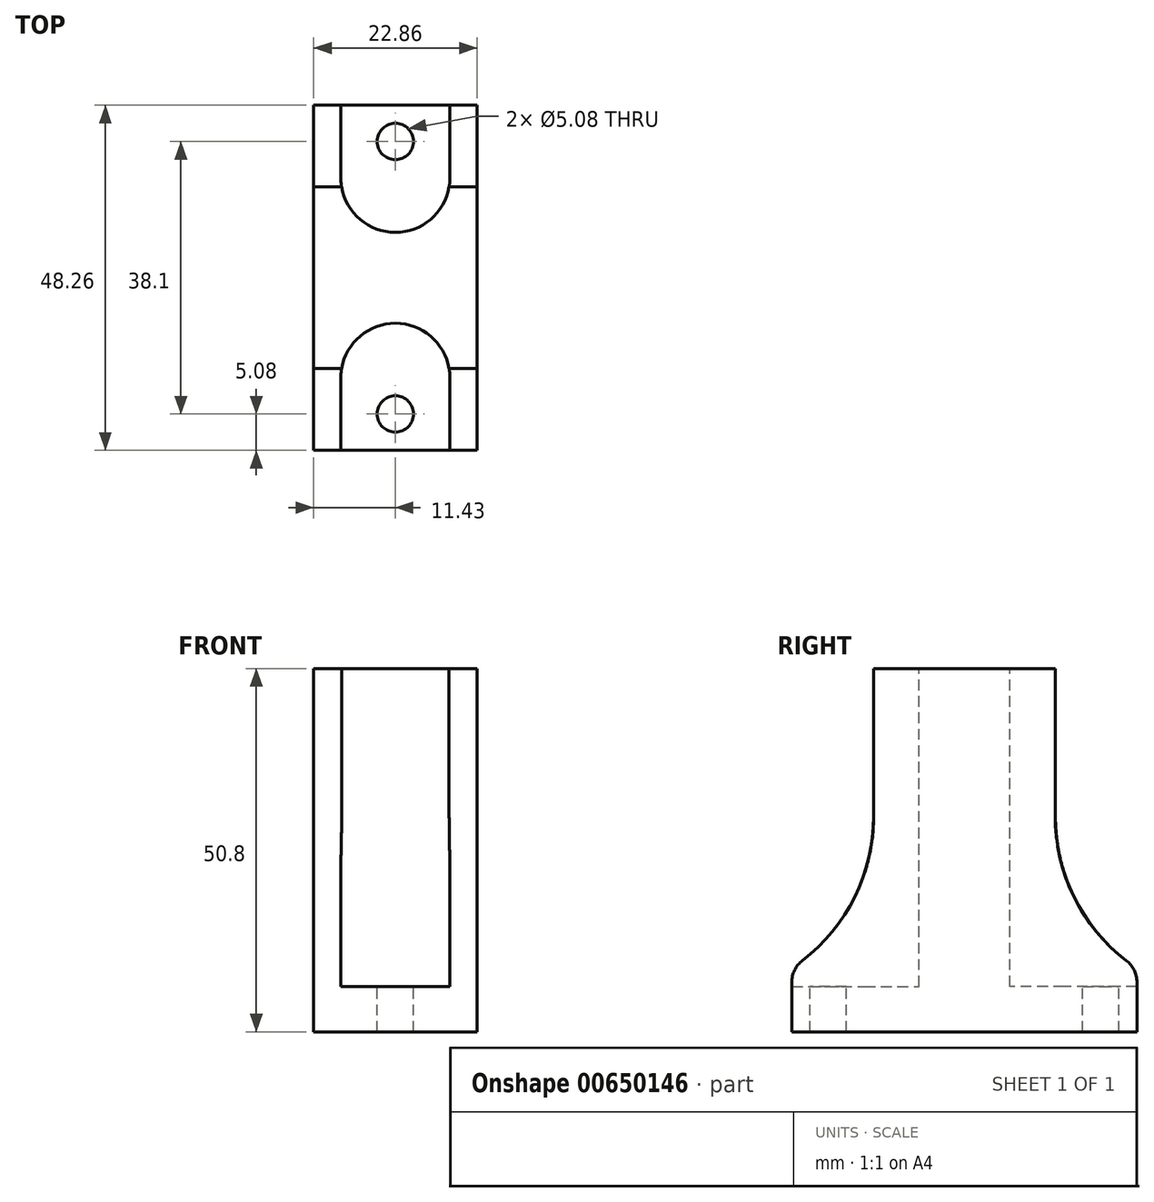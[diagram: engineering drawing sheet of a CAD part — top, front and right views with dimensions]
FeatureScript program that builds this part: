
annotation { "Feature Type Name" : "Feature", "Feature Type Description" : "" }
export const myFeature = defineFeature(function(context is Context, id is Id, definition is map)
    precondition{}
    {
        {
            var Q0;
            Q0=qCreatedBy(makeId("Top.planeOp"),FACE);
            var sketch = newSketch(context, id + "F0", { "sketchPlane" : qUnion([Q0])});
            skLineSegment(sketch, "E0.bottom", {"start": v(-11.43, 24.13) * mm, "end": v(11.43, 24.13) * mm});
            skLineSegment(sketch, "E0.top", {"start": v(-11.43, -24.13) * mm, "end": v(11.43, -24.13) * mm});
            skLineSegment(sketch, "E0.left", {"start": v(-11.43, 24.13) * mm, "end": v(-11.43, -24.13) * mm});
            skLineSegment(sketch, "E0.right", {"start": v(11.43, 24.13) * mm, "end": v(11.43, -24.13) * mm});
            skLineSegment(sketch, "E1", {"start": v(-11.43, -24.13) * mm, "end": v(11.43, 24.13) * mm, "construction": true});
            skSolve(sketch);
        }
        {
            var Q0;
            Q0 = qSketchRegion(id + "F0", true);
            extrude(context, id + "F1", {"entities" : qUnion([Q0]), "depth" : 50.8 * mm, "offsetDistance" : 25.4 * mm});
        }
        {
            var Q0;
            Q0=makeQuery(id+"F1.opExtrude","CAP_FACE",FACE,{"disambiguationData":[OSD([sQuery(id+"F0.wireOp",EDGE,"E0.bottom"),sQuery(id+"F0.wireOp",EDGE,"E0.top"),sQuery(id+"F0.wireOp",EDGE,"E0.left"),sQuery(id+"F0.wireOp",EDGE,"E0.right")])],"isStart":false});
            var sketch = newSketch(context, id + "F2", { "sketchPlane" : qUnion([Q0])});
            skLineSegment(sketch, "E2.bottom", {"start": v(-11.43, 12.7) * mm, "end": v(11.43, 12.7) * mm, "construction": true});
            skLineSegment(sketch, "E2.top", {"start": v(-11.43, -12.7) * mm, "end": v(11.43, -12.7) * mm, "construction": true});
            skLineSegment(sketch, "E2.left", {"start": v(-11.43, 12.7) * mm, "end": v(-11.43, -12.7) * mm, "construction": true});
            skLineSegment(sketch, "E2.right", {"start": v(11.43, 12.7) * mm, "end": v(11.43, -12.7) * mm, "construction": true});
            skLineSegment(sketch, "E3", {"start": v(-11.43, 12.7) * mm, "end": v(11.43, -12.7) * mm, "construction": true});
            skLineSegment(sketch, "E4.bottom", {"start": v(-11.43, 24.13) * mm, "end": v(11.43, 24.13) * mm});
            skLineSegment(sketch, "E4.top", {"start": v(-11.43, 12.7) * mm, "end": v(11.43, 12.7) * mm});
            skLineSegment(sketch, "E4.left", {"start": v(-11.43, 24.13) * mm, "end": v(-11.43, 12.7) * mm});
            skLineSegment(sketch, "E4.right", {"start": v(11.43, 24.13) * mm, "end": v(11.43, 12.7) * mm});
            skLineSegment(sketch, "E5.bottom", {"start": v(-11.43, -24.13) * mm, "end": v(11.43, -24.13) * mm});
            skLineSegment(sketch, "E5.top", {"start": v(-11.43, -12.7) * mm, "end": v(11.43, -12.7) * mm});
            skLineSegment(sketch, "E5.left", {"start": v(-11.43, -24.13) * mm, "end": v(-11.43, -12.7) * mm});
            skLineSegment(sketch, "E5.right", {"start": v(11.43, -24.13) * mm, "end": v(11.43, -12.7) * mm});
            skLineSegment(sketch, "E6.bottom", {"start": v(-7.62, 12.7) * mm, "end": v(7.62, 12.7) * mm});
            skLineSegment(sketch, "E6.top", {"start": v(-7.62, 6.35) * mm, "end": v(7.62, 6.35) * mm});
            skLineSegment(sketch, "E6.left", {"start": v(-7.62, 12.7) * mm, "end": v(-7.62, 6.35) * mm});
            skLineSegment(sketch, "E6.right", {"start": v(7.62, 12.7) * mm, "end": v(7.62, 6.35) * mm});
            skLineSegment(sketch, "E7.bottom", {"start": v(-7.62, -12.7) * mm, "end": v(7.62, -12.7) * mm});
            skLineSegment(sketch, "E7.top", {"start": v(-7.62, -6.35) * mm, "end": v(7.62, -6.35) * mm});
            skLineSegment(sketch, "E7.left", {"start": v(-7.62, -12.7) * mm, "end": v(-7.62, -6.35) * mm});
            skLineSegment(sketch, "E7.right", {"start": v(7.62, -12.7) * mm, "end": v(7.62, -6.35) * mm});
            skSolve(sketch);
        }
        {
            var Q0;
            Q0 = qSketchRegion(id + "F2", true);
            extrude(context, id + "F3", {"entities" : qUnion([Q0]), "operationType" : NewBodyOperationType.REMOVE, "oppositeDirection" : true, "depth" : 41.9 * mm, "offsetDistance" : 25.4 * mm});
        }
        {
            var Q0;
            {var subQ0=sQuery(id+"F2.wireOp",EDGE,"E5.top");Q0=makeQuery(id+"F3.boolean.opBoolean","COPY",EDGE,{"derivedFrom":makeQuery(id+"F3.opExtrude","CAP_EDGE",EDGE,{"disambiguationData":[OSD([subQ0]),TDD([makeQuery(id+"F2.imprint","IMPRINT",EDGE,{"disambiguationData":[TD([[makeQuery(id+"F2.imprint","INTERSECT",VERTEX,{"derivedFrom":[makeQuery(id+"F1.opExtrude","CAP_EDGE",EDGE,{"disambiguationData":[OSD([sQuery(id+"F0.wireOp",EDGE,"E0.left")])],"isStart":false}),subQ0,sQuery(id+"F2.wireOp",EDGE,"E5.left")]}),-1.0]])],"derivedFrom":subQ0})])],"isStart":false})});}
            var Q1;
            {var subQ0=sQuery(id+"F2.wireOp",EDGE,"E5.top");Q1=makeQuery(id+"F3.boolean.opBoolean","COPY",EDGE,{"derivedFrom":makeQuery(id+"F3.opExtrude","CAP_EDGE",EDGE,{"disambiguationData":[OSD([subQ0]),TDD([makeQuery(id+"F2.imprint","IMPRINT",EDGE,{"disambiguationData":[TD([[makeQuery(id+"F2.imprint","INTERSECT",VERTEX,{"derivedFrom":[makeQuery(id+"F1.opExtrude","CAP_EDGE",EDGE,{"disambiguationData":[OSD([sQuery(id+"F0.wireOp",EDGE,"E0.right")])],"isStart":false}),subQ0,sQuery(id+"F2.wireOp",EDGE,"E5.right")]}),1.0]])],"derivedFrom":subQ0})])],"isStart":false})});}
            var Q2;
            {var subQ0=sQuery(id+"F2.wireOp",EDGE,"E4.top");Q2=makeQuery(id+"F3.boolean.opBoolean","COPY",EDGE,{"derivedFrom":makeQuery(id+"F3.opExtrude","CAP_EDGE",EDGE,{"disambiguationData":[OSD([subQ0]),TDD([makeQuery(id+"F2.imprint","IMPRINT",EDGE,{"disambiguationData":[TD([[makeQuery(id+"F2.imprint","INTERSECT",VERTEX,{"derivedFrom":[makeQuery(id+"F1.opExtrude","CAP_EDGE",EDGE,{"disambiguationData":[OSD([sQuery(id+"F0.wireOp",EDGE,"E0.left")])],"isStart":false}),subQ0,sQuery(id+"F2.wireOp",EDGE,"E4.left")]}),-1.0]])],"derivedFrom":subQ0})])],"isStart":false})});}
            var Q3;
            {var subQ0=sQuery(id+"F2.wireOp",EDGE,"E4.top");Q3=makeQuery(id+"F3.boolean.opBoolean","COPY",EDGE,{"derivedFrom":makeQuery(id+"F3.opExtrude","CAP_EDGE",EDGE,{"disambiguationData":[OSD([subQ0]),TDD([makeQuery(id+"F2.imprint","IMPRINT",EDGE,{"disambiguationData":[TD([[makeQuery(id+"F2.imprint","INTERSECT",VERTEX,{"derivedFrom":[makeQuery(id+"F1.opExtrude","CAP_EDGE",EDGE,{"disambiguationData":[OSD([sQuery(id+"F0.wireOp",EDGE,"E0.right")])],"isStart":false}),subQ0,sQuery(id+"F2.wireOp",EDGE,"E4.right")]}),1.0]])],"derivedFrom":subQ0})])],"isStart":false})});}
            fillet(context, id + "F4", {"entities" : qUnion([Q0, Q1, Q2, Q3]), "radius" : 25.4 * mm, "tangentPropagation" : true, "allowEdgeOverflow" : false});
        }
        {
            var Q0;
            Q0=makeQuery(id+"F3.boolean.opBoolean","COPY",EDGE,{"derivedFrom":makeQuery(id+"F3.opExtrude","SWEPT_EDGE",EDGE,{"disambiguationData":[OSD([sQuery(id+"F2.wireOp",EDGE,"E6.top"),sQuery(id+"F2.wireOp",EDGE,"E6.right")])]})});
            var Q1;
            Q1=makeQuery(id+"F3.boolean.opBoolean","COPY",EDGE,{"derivedFrom":makeQuery(id+"F3.opExtrude","SWEPT_EDGE",EDGE,{"disambiguationData":[OSD([sQuery(id+"F2.wireOp",EDGE,"E6.top"),sQuery(id+"F2.wireOp",EDGE,"E6.left")])]})});
            var Q2;
            Q2=makeQuery(id+"F3.boolean.opBoolean","COPY",EDGE,{"derivedFrom":makeQuery(id+"F3.opExtrude","SWEPT_EDGE",EDGE,{"disambiguationData":[OSD([sQuery(id+"F2.wireOp",EDGE,"E7.top"),sQuery(id+"F2.wireOp",EDGE,"E7.right")])]})});
            var Q3;
            Q3=makeQuery(id+"F3.boolean.opBoolean","COPY",EDGE,{"derivedFrom":makeQuery(id+"F3.opExtrude","SWEPT_EDGE",EDGE,{"disambiguationData":[OSD([sQuery(id+"F2.wireOp",EDGE,"E7.top"),sQuery(id+"F2.wireOp",EDGE,"E7.left")])]})});
            fillet(context, id + "F5", {"entities" : qUnion([Q0, Q1, Q2, Q3]), "radius" : 7.62 * mm, "tangentPropagation" : true, "allowEdgeOverflow" : false});
        }
        {
            var Q0;
            Q0=makeQuery(id+"F3.boolean.opBoolean","COPY",FACE,{"derivedFrom":makeQuery(id+"F3.opExtrude","CAP_FACE",FACE,{"disambiguationData":[OSD([sQuery(id+"F2.wireOp",EDGE,"E4.bottom"),sQuery(id+"F2.wireOp",EDGE,"E4.top"),sQuery(id+"F2.wireOp",EDGE,"E4.left"),sQuery(id+"F2.wireOp",EDGE,"E4.right"),sQuery(id+"F2.wireOp",EDGE,"E6.top"),sQuery(id+"F2.wireOp",EDGE,"E6.left"),sQuery(id+"F2.wireOp",EDGE,"E6.right")])],"isStart":false})});
            var Q1;
            Q1=makeQuery(id+"F3.boolean.opBoolean","COPY",FACE,{"derivedFrom":makeQuery(id+"F3.opExtrude","CAP_FACE",FACE,{"disambiguationData":[OSD([sQuery(id+"F2.wireOp",EDGE,"E5.bottom"),sQuery(id+"F2.wireOp",EDGE,"E5.top"),sQuery(id+"F2.wireOp",EDGE,"E5.left"),sQuery(id+"F2.wireOp",EDGE,"E5.right"),sQuery(id+"F2.wireOp",EDGE,"E7.top"),sQuery(id+"F2.wireOp",EDGE,"E7.left"),sQuery(id+"F2.wireOp",EDGE,"E7.right")])],"isStart":false})});
            extrude(context, id + "F6", {"entities" : qUnion([Q0, Q1]), "operationType" : NewBodyOperationType.REMOVE, "oppositeDirection" : true, "depth" : 2.54 * mm, "offsetDistance" : 25.4 * mm});
        }
        {
            var Q0;
            {var subQ0=sQuery(id+"F2.wireOp",EDGE,"E4.top");Q0=makeQuery(id+"F4.opFillet","BLEND_EDGE",EDGE,{"blendedFrom":[makeQuery(id+"F3.boolean.opBoolean","COPY",EDGE,{"derivedFrom":makeQuery(id+"F3.opExtrude","CAP_EDGE",EDGE,{"disambiguationData":[OSD([subQ0]),TDD([makeQuery(id+"F2.imprint","IMPRINT",EDGE,{"disambiguationData":[TD([[makeQuery(id+"F2.imprint","INTERSECT",VERTEX,{"derivedFrom":[makeQuery(id+"F1.opExtrude","CAP_EDGE",EDGE,{"disambiguationData":[OSD([sQuery(id+"F0.wireOp",EDGE,"E0.right")])],"isStart":false}),subQ0,sQuery(id+"F2.wireOp",EDGE,"E4.right")]}),1.0]])],"derivedFrom":subQ0})])],"isStart":false})}),makeQuery(id+"F1.opExtrude","SWEPT_FACE",FACE,{"disambiguationData":[OSD([sQuery(id+"F0.wireOp",EDGE,"E0.bottom")])]})],"blendedInto":[makeQuery(id+"F1.opExtrude","SWEPT_FACE",FACE,{"disambiguationData":[OSD([sQuery(id+"F0.wireOp",EDGE,"E0.bottom")])]})]});}
            var Q1;
            {var subQ0=sQuery(id+"F2.wireOp",EDGE,"E4.top");Q1=makeQuery(id+"F4.opFillet","BLEND_EDGE",EDGE,{"blendedFrom":[makeQuery(id+"F3.boolean.opBoolean","COPY",EDGE,{"derivedFrom":makeQuery(id+"F3.opExtrude","CAP_EDGE",EDGE,{"disambiguationData":[OSD([subQ0]),TDD([makeQuery(id+"F2.imprint","IMPRINT",EDGE,{"disambiguationData":[TD([[makeQuery(id+"F2.imprint","INTERSECT",VERTEX,{"derivedFrom":[makeQuery(id+"F1.opExtrude","CAP_EDGE",EDGE,{"disambiguationData":[OSD([sQuery(id+"F0.wireOp",EDGE,"E0.left")])],"isStart":false}),subQ0,sQuery(id+"F2.wireOp",EDGE,"E4.left")]}),-1.0]])],"derivedFrom":subQ0})])],"isStart":false})}),makeQuery(id+"F1.opExtrude","SWEPT_FACE",FACE,{"disambiguationData":[OSD([sQuery(id+"F0.wireOp",EDGE,"E0.bottom")])]})],"blendedInto":[makeQuery(id+"F1.opExtrude","SWEPT_FACE",FACE,{"disambiguationData":[OSD([sQuery(id+"F0.wireOp",EDGE,"E0.bottom")])]})]});}
            var Q2;
            {var subQ0=sQuery(id+"F2.wireOp",EDGE,"E5.top");Q2=makeQuery(id+"F4.opFillet","BLEND_EDGE",EDGE,{"blendedFrom":[makeQuery(id+"F3.boolean.opBoolean","COPY",EDGE,{"derivedFrom":makeQuery(id+"F3.opExtrude","CAP_EDGE",EDGE,{"disambiguationData":[OSD([subQ0]),TDD([makeQuery(id+"F2.imprint","IMPRINT",EDGE,{"disambiguationData":[TD([[makeQuery(id+"F2.imprint","INTERSECT",VERTEX,{"derivedFrom":[makeQuery(id+"F1.opExtrude","CAP_EDGE",EDGE,{"disambiguationData":[OSD([sQuery(id+"F0.wireOp",EDGE,"E0.left")])],"isStart":false}),subQ0,sQuery(id+"F2.wireOp",EDGE,"E5.left")]}),-1.0]])],"derivedFrom":subQ0})])],"isStart":false})}),makeQuery(id+"F1.opExtrude","SWEPT_FACE",FACE,{"disambiguationData":[OSD([sQuery(id+"F0.wireOp",EDGE,"E0.top")])]})],"blendedInto":[makeQuery(id+"F1.opExtrude","SWEPT_FACE",FACE,{"disambiguationData":[OSD([sQuery(id+"F0.wireOp",EDGE,"E0.top")])]})]});}
            var Q3;
            {var subQ0=sQuery(id+"F2.wireOp",EDGE,"E5.top");Q3=makeQuery(id+"F4.opFillet","BLEND_EDGE",EDGE,{"blendedFrom":[makeQuery(id+"F3.boolean.opBoolean","COPY",EDGE,{"derivedFrom":makeQuery(id+"F3.opExtrude","CAP_EDGE",EDGE,{"disambiguationData":[OSD([subQ0]),TDD([makeQuery(id+"F2.imprint","IMPRINT",EDGE,{"disambiguationData":[TD([[makeQuery(id+"F2.imprint","INTERSECT",VERTEX,{"derivedFrom":[makeQuery(id+"F1.opExtrude","CAP_EDGE",EDGE,{"disambiguationData":[OSD([sQuery(id+"F0.wireOp",EDGE,"E0.right")])],"isStart":false}),subQ0,sQuery(id+"F2.wireOp",EDGE,"E5.right")]}),1.0]])],"derivedFrom":subQ0})])],"isStart":false})}),makeQuery(id+"F1.opExtrude","SWEPT_FACE",FACE,{"disambiguationData":[OSD([sQuery(id+"F0.wireOp",EDGE,"E0.top")])]})],"blendedInto":[makeQuery(id+"F1.opExtrude","SWEPT_FACE",FACE,{"disambiguationData":[OSD([sQuery(id+"F0.wireOp",EDGE,"E0.top")])]})]});}
            fillet(context, id + "F7", {"entities" : qUnion([Q0, Q1, Q2, Q3]), "radius" : 3.8 * mm, "tangentPropagation" : true, "allowEdgeOverflow" : false});
        }
        {
            var Q0;
            Q0=makeQuery(id+"F6.boolean.opBoolean","COPY",FACE,{"derivedFrom":makeQuery(id+"F6.opExtrude","CAP_FACE",FACE,{"disambiguationData":[OSD([sQuery(id+"F2.wireOp",EDGE,"E5.bottom"),sQuery(id+"F2.wireOp",EDGE,"E5.top"),sQuery(id+"F2.wireOp",EDGE,"E5.left"),sQuery(id+"F2.wireOp",EDGE,"E5.right"),sQuery(id+"F2.wireOp",EDGE,"E7.top"),sQuery(id+"F2.wireOp",EDGE,"E7.left"),sQuery(id+"F2.wireOp",EDGE,"E7.right")])],"isStart":false})});
            var sketch = newSketch(context, id + "F8", { "sketchPlane" : qUnion([Q0])});
            skLineSegment(sketch, "E8", {"start": v(0, -24.13) * mm, "end": v(0, -19.05) * mm, "construction": true});
            skCircle(sketch, "E9", {"center": v(0, -19.05) * mm, "radius": 2.54 * mm});
            skCircle(sketch, "E10.MirrorC", {"center": v(0, 19.05) * mm, "radius": 2.54 * mm});
            skSolve(sketch);
        }
        {
            var Q0;
            Q0 = qSketchRegion(id + "F8", true);
            extrude(context, id + "F9", {"entities" : qUnion([Q0]), "operationType" : NewBodyOperationType.REMOVE, "oppositeDirection" : true, "depth" : 25.4 * mm, "offsetDistance" : 25.4 * mm});
        }
    });
